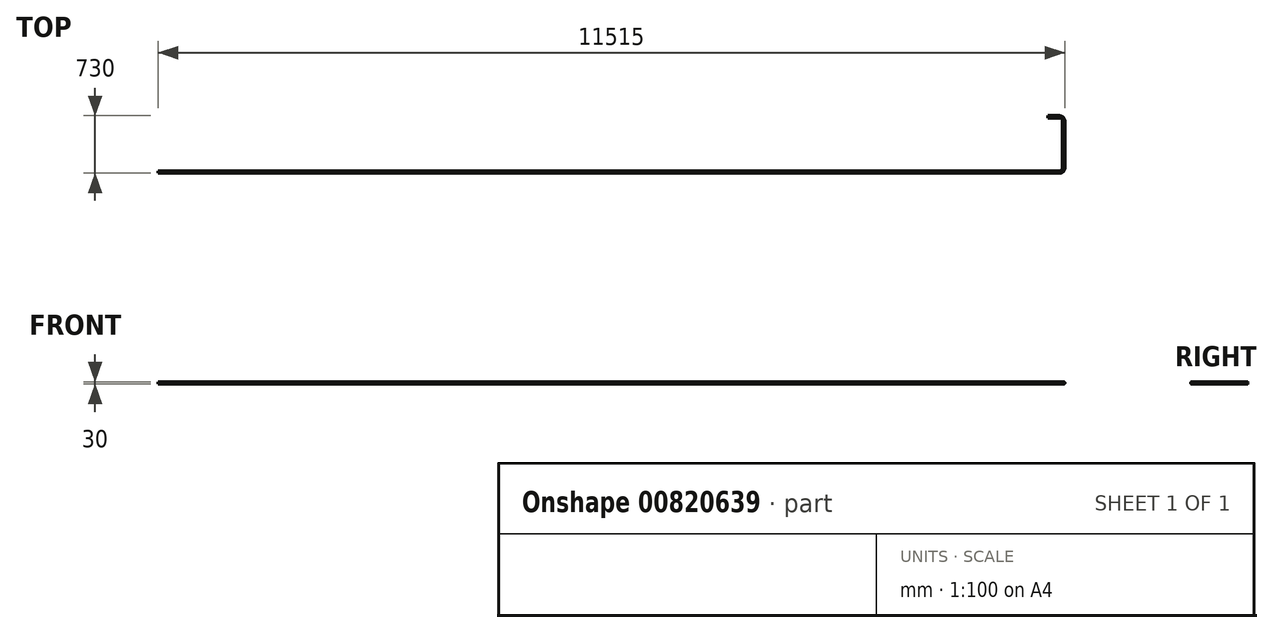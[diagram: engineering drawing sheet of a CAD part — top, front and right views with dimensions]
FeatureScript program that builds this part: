
annotation { "Feature Type Name" : "Feature", "Feature Type Description" : "" }
export const myFeature = defineFeature(function(context is Context, id is Id, definition is map)
    precondition{}
    {
        {
            var Q0;
            Q0=qCreatedBy(makeId("Top.planeOp"),FACE);
            var sketch = newSketch(context, id + "F0", { "sketchPlane" : qUnion([Q0])});
            skLineSegment(sketch, "E0", {"start": v(0, 0) * mm, "end": v(150, 0) * mm});
            skLineSegment(sketch, "E1", {"start": v(200, -50) * mm, "end": v(200, -650) * mm});
            skLineSegment(sketch, "E2", {"start": v(150, -700) * mm, "end": v(-11300, -700) * mm});
            skPoint(sketch, "E3.visualSharp", {"position": v(200, 0) * mm});
            skArc(sketch, "E3.filletArc", {"start": v(200, -50) * mm, "mid": v(185.36, -14.64) * mm, "end": v(150, 0) * mm});
            skPoint(sketch, "E4.visualSharp", {"position": v(200, -700) * mm});
            skArc(sketch, "E4.filletArc", {"start": v(150, -700) * mm, "mid": v(185.36, -685.36) * mm, "end": v(200, -650) * mm});
            skSolve(sketch);
        }
        {
            var Q0;
            Q0=qCreatedBy(makeId("Right.planeOp"),FACE);
            var sketch = newSketch(context, id + "F1", { "sketchPlane" : qUnion([Q0])});
            skCircle(sketch, "E5", {"center": v(0, 0) * mm, "radius": 15 * mm});
            skSolve(sketch);
        }
        {
            var Q0;
            Q0=makeQuery(id+"F1.imprint","IMPRINT",FACE,{"disambiguationData":[TD([[makeQuery(id+"F1.imprint","IMPRINT",EDGE,{"derivedFrom":sQuery(id+"F1.wireOp",EDGE,"E5")}),1.0]])]});
            var Q1;
            Q1=sQuery(id+"F0.wireOp",EDGE,"E0");
            var Q2;
            Q2=sQuery(id+"F0.wireOp",EDGE,"E3.filletArc");
            var Q3;
            Q3=sQuery(id+"F0.wireOp",EDGE,"E1");
            var Q4;
            Q4=sQuery(id+"F0.wireOp",EDGE,"E4.filletArc");
            var Q5;
            Q5=sQuery(id+"F0.wireOp",EDGE,"E2");
            sweep(context, id + "F2", {"profiles" : qUnion([Q0]), "path" : qUnion([Q1, Q2, Q3, Q4, Q5])});
        }
    });
